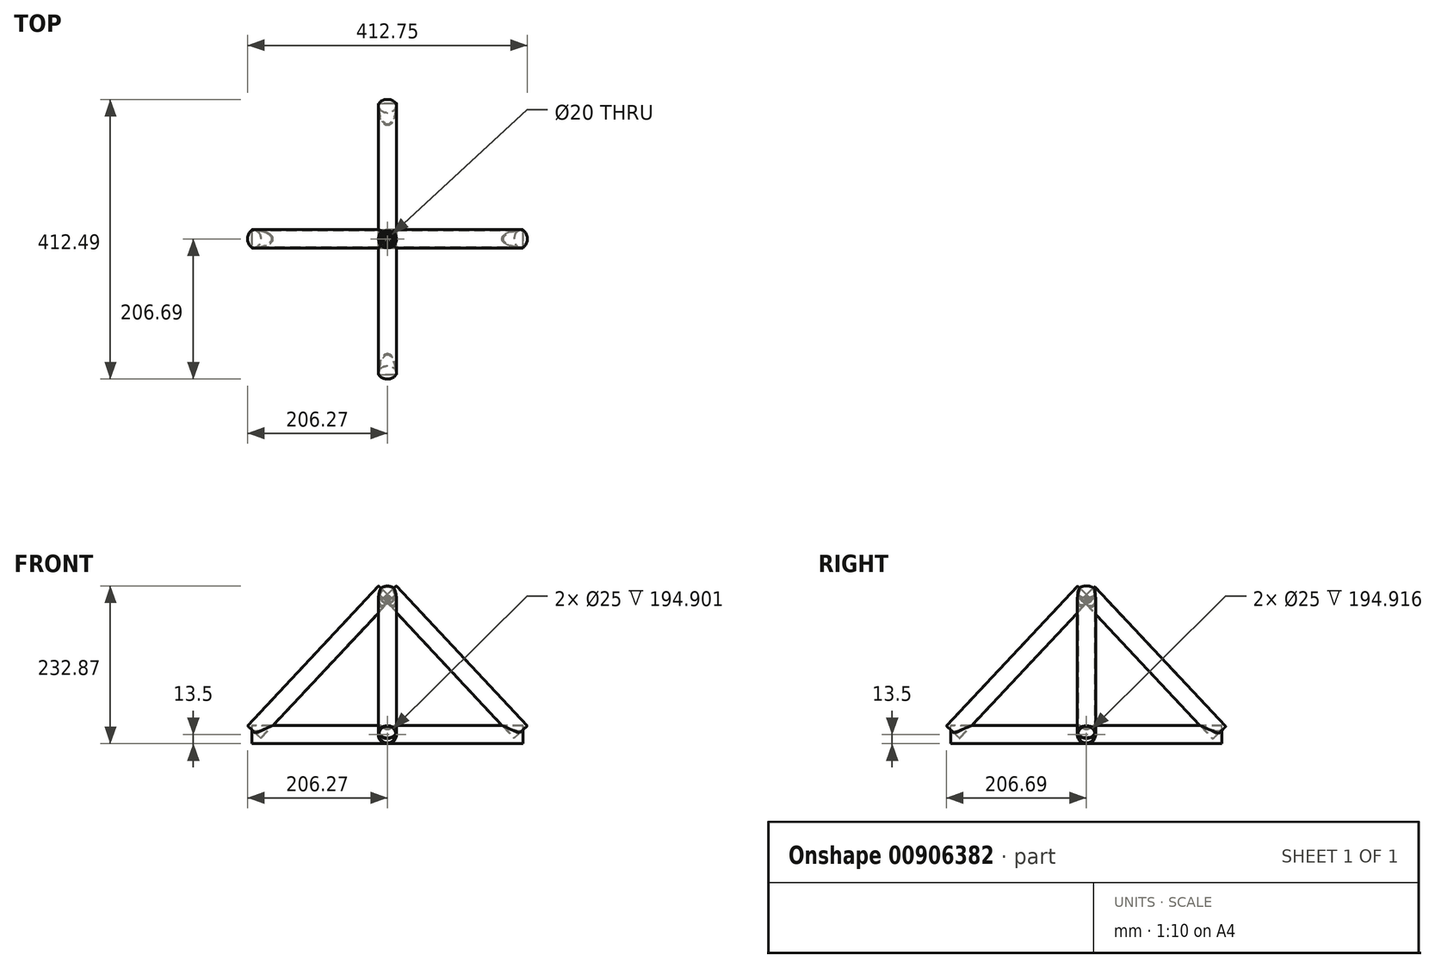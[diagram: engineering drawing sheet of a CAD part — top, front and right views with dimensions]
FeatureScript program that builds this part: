
annotation { "Feature Type Name" : "Feature", "Feature Type Description" : "" }
export const myFeature = defineFeature(function(context is Context, id is Id, definition is map)
    precondition{}
    {
        {
            var Q0;
            Q0=qCreatedBy(makeId("Top.planeOp"),FACE);
            var sketch = newSketch(context, id + "F0", { "sketchPlane" : qUnion([Q0])});
            skCircle(sketch, "E0", {"center": v(0, 0) * mm, "radius": 12.5 * mm});
            skCircle(sketch, "E1", {"center": v(0, 0) * mm, "radius": 13.5 * mm});
            skSolve(sketch);
        }
        {
            var Q0;
            Q0=sQuery(id+"F0.wireOp",EDGE,"E0");
            var Q1;
            Q1=sQuery(id+"F0.wireOp",EDGE,"E1");
            extrude(context, id + "F1", {"bodyType" : ToolBodyType.SURFACE, "surfaceEntities" : qUnion([Q0, Q1]), "depth" : 213.5 * mm, "offsetDistance" : 25 * mm});
        }
        {
            var Q0;
            Q0=qCreatedBy(makeId("Front.planeOp"),FACE);
            var sketch = newSketch(context, id + "F2", { "sketchPlane" : qUnion([Q0])});
            skCircle(sketch, "E2", {"center": v(0, 0) * mm, "radius": 13.5 * mm});
            skCircle(sketch, "E3", {"center": v(0, 0) * mm, "radius": 12.5 * mm});
            skSolve(sketch);
        }
        {
            var Q0;
            Q0 = qSketchRegion(id + "F2", true);
            extrude(context, id + "F3", {"entities" : qUnion([Q0]), "oppositeDirection" : true, "depth" : 200 * mm, "offsetDistance" : 25 * mm, "hasSecondDirection" : true, "secondDirectionOppositeDirection" : false, "secondDirectionDepth" : 200 * mm});
        }
        {
            var Q0;
            Q0=qCreatedBy(makeId("Right.planeOp"),FACE);
            var sketch = newSketch(context, id + "F4", { "sketchPlane" : qUnion([Q0])});
            skCircle(sketch, "E4", {"center": v(0, 0) * mm, "radius": 12.5 * mm});
            skCircle(sketch, "E5", {"center": v(0, 0) * mm, "radius": 13.5 * mm});
            skSolve(sketch);
        }
        {
            var Q0;
            Q0 = qSketchRegion(id + "F4", true);
            extrude(context, id + "F5", {"entities" : qUnion([Q0]), "operationType" : NewBodyOperationType.ADD, "depth" : 200 * mm, "offsetDistance" : 25 * mm, "hasSecondDirection" : true, "secondDirectionOppositeDirection" : true, "secondDirectionDepth" : 200 * mm});
        }
        {
            var Q0;
            Q0=qCreatedBy(makeId("Front.planeOp"),FACE);
            var sketch = newSketch(context, id + "F6", { "sketchPlane" : qUnion([Q0])});
            skPoint(sketch, "E6", {"position": v(0, 213.55) * mm});
            skPoint(sketch, "E7", {"position": v(-199.67, 0) * mm});
            skLineSegment(sketch, "E8", {"start": v(0, 213.55) * mm, "end": v(-199.67, 0) * mm});
            skPoint(sketch, "E9", {"position": v(199.78, 0) * mm});
            skLineSegment(sketch, "E10", {"start": v(199.78, 0) * mm, "end": v(0, 213.55) * mm});
            skSolve(sketch);
        }
        {
            var Q0;
            Q0=qCreatedBy(makeId("Right.planeOp"),FACE);
            var sketch = newSketch(context, id + "F7", { "sketchPlane" : qUnion([Q0])});
            skPoint(sketch, "E11", {"position": v(200.42, 0) * mm});
            skPoint(sketch, "E12", {"position": v(-200.17, 0) * mm});
            skLineSegment(sketch, "E13", {"start": v(200.42, 0) * mm, "end": v(0, 213.21) * mm});
            skLineSegment(sketch, "E14", {"start": v(0, 213.21) * mm, "end": v(-200.17, 0) * mm});
            skSolve(sketch);
        }
        {
            var Q0;
            Q0=sQuery(id+"F6.wireOp",EDGE,"E10");
            cPlane(context, id + "F8", {"entities" : qUnion([Q0]), "cplaneType" : CPlaneType.MID_PLANE, "offset" : 25 * mm, "width" : 150 * mm, "height" : 150 * mm});
        }
        {
            var Q0;
            Q0=sQuery(id+"F7.wireOp",EDGE,"E13");
            cPlane(context, id + "F9", {"entities" : qUnion([Q0]), "cplaneType" : CPlaneType.MID_PLANE, "offset" : 25 * mm, "width" : 150 * mm, "height" : 150 * mm});
        }
        {
            var Q0;
            Q0=sQuery(id+"F6.wireOp",EDGE,"E8");
            cPlane(context, id + "F10", {"entities" : qUnion([Q0]), "cplaneType" : CPlaneType.MID_PLANE, "offset" : 25 * mm, "width" : 150 * mm, "height" : 150 * mm});
        }
        {
            var Q0;
            Q0=sQuery(id+"F7.wireOp",EDGE,"E14");
            cPlane(context, id + "F11", {"entities" : qUnion([Q0]), "cplaneType" : CPlaneType.MID_PLANE, "offset" : 25 * mm, "width" : 150 * mm, "height" : 150 * mm});
        }
        {
            var Q0;
            Q0=qCreatedBy(id+"F9.planeOp",FACE);
            var sketch = newSketch(context, id + "F12", { "sketchPlane" : qUnion([Q0])});
            skCircle(sketch, "E15", {"center": v(0, 144.53) * mm, "radius": 12.5 * mm});
            skCircle(sketch, "E16", {"center": v(0, 144.53) * mm, "radius": 13.5 * mm});
            skSolve(sketch);
        }
        {
            var Q0;
            Q0 = qSketchRegion(id + "F12", true);
            extrude(context, id + "F13", {"entities" : qUnion([Q0]), "operationType" : NewBodyOperationType.ADD, "depth" : 141.4 * mm, "offsetDistance" : 25 * mm, "hasSecondDirection" : true, "secondDirectionOppositeDirection" : true, "secondDirectionDepth" : 141.4 * mm});
        }
        {
            var Q0;
            Q0=qCreatedBy(id+"F10.planeOp",FACE);
            var sketch = newSketch(context, id + "F14", { "sketchPlane" : qUnion([Q0])});
            skCircle(sketch, "E17", {"center": v(-145.85, 0) * mm, "radius": 13.5 * mm});
            skCircle(sketch, "E18", {"center": v(-145.85, 0) * mm, "radius": 12.5 * mm});
            skSolve(sketch);
        }
        {
            var Q0;
            Q0 = qSketchRegion(id + "F14", true);
            extrude(context, id + "F15", {"entities" : qUnion([Q0]), "operationType" : NewBodyOperationType.ADD, "depth" : 141.4 * mm, "offsetDistance" : 25 * mm, "hasSecondDirection" : true, "secondDirectionOppositeDirection" : true, "secondDirectionDepth" : 141.4 * mm});
        }
        {
            var Q0;
            Q0=qCreatedBy(id+"F8.planeOp",FACE);
            var sketch = newSketch(context, id + "F16", { "sketchPlane" : qUnion([Q0])});
            skCircle(sketch, "E19", {"center": v(146.06, 0) * mm, "radius": 13.5 * mm});
            skCircle(sketch, "E20", {"center": v(146.06, 0) * mm, "radius": 12.5 * mm});
            skSolve(sketch);
        }
        {
            var Q0;
            Q0 = qSketchRegion(id + "F16", true);
            extrude(context, id + "F17", {"entities" : qUnion([Q0]), "operationType" : NewBodyOperationType.ADD, "depth" : 141.4 * mm, "offsetDistance" : 25 * mm, "hasSecondDirection" : true, "secondDirectionOppositeDirection" : true, "secondDirectionDepth" : 141.4 * mm});
        }
        {
            var Q0;
            Q0=qCreatedBy(id+"F11.planeOp",FACE);
            var sketch = newSketch(context, id + "F18", { "sketchPlane" : qUnion([Q0])});
            skCircle(sketch, "E21", {"center": v(0, 145.9) * mm, "radius": 12.5 * mm});
            skCircle(sketch, "E22", {"center": v(0, 145.9) * mm, "radius": 13.5 * mm});
            skSolve(sketch);
        }
        {
            var Q0;
            Q0 = qSketchRegion(id + "F18", true);
            extrude(context, id + "F19", {"entities" : qUnion([Q0]), "operationType" : NewBodyOperationType.ADD, "depth" : 141.4 * mm, "offsetDistance" : 25 * mm, "hasSecondDirection" : true, "secondDirectionOppositeDirection" : true, "secondDirectionDepth" : 141.4 * mm});
        }
        {
            var Q0;
            Q0=qCreatedBy(makeId("Top.planeOp"),FACE);
            var sketch = newSketch(context, id + "F20", { "sketchPlane" : qUnion([Q0])});
            skCircle(sketch, "E23", {"center": v(0, 0) * mm, "radius": 10 * mm});
            skSolve(sketch);
        }
        {
            var Q0;
            Q0 = qSketchRegion(id + "F20", true);
            extrude(context, id + "F21", {"entities" : qUnion([Q0]), "operationType" : NewBodyOperationType.REMOVE, "depth" : 50 * mm, "offsetDistance" : 25 * mm});
        }
    });
